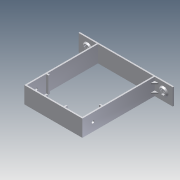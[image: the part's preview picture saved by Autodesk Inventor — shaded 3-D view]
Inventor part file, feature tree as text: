
AUTODESK INVENTOR PART (.ipt)
format: ipt  version: 2011 (Build 150239000, 239)  size: 209,920 bytes
history: native  units: mm
features: extrude x5, sketch x5, plane x1, rib x1, pattern_linear x1, draft x1, mirror x1
ambient origin geometry x8: Origin, YZ Plane, XZ Plane, XY Plane, X Axis, Y Axis, Z Axis, Center Point
bodies: Solid1 (feature_tree)
feature tree (15):
  extrude  "Extrusion1"  Depth=1.75mm
  extrude  "Extrusion2"  Depth=22.75mm
  extrude  "Extrusion3"  Depth=36.5mm
  plane  "Work Plane1"
  rib  "Rib1"
  pattern_linear  "Rectangular Pattern1"  Spacing1=21.0mm  [1 undecoded]
  sketch  "Sketch6"  dims[d9=3.4mm d10=21.0mm d11=0.0mm d12=23.3mm d13=3.4mm d14=21.0mm d15=0.0mm d16=1.75mm d17=3.0mm d18=21.6mm d21=5.25mm d22=45.0deg d24=1.0mm d25=1.75mm d26=0.0mm d27=20.0mm d29=10.5mm d30=4.5mm d31=1.75mm d32=5.6mm d33=1.5mm d34=0.75mm d35=0.0mm d36=1.55mm d37=0.0mm d38=45.0deg d39=1.75mm d40=3.0mm d41=23.9mm]
  extrude  "Extrusion5"  Depth=23.3mm
  extrude  "Extrusion6"  Depth=3.4mm
  draft  "FaceDraft1"
  mirror  "Mirror5"
  sketch  "Sketch1"  dims[d0=1.75mm d1=1.75mm]
  sketch  "Sketch2"  dims[d2=1.75mm d4=22.75mm]
  sketch  "Sketch3"  dims[d5=21.0mm d6=0.0mm d7=36.5mm]
  sketch  "Sketch5"  dims[d8=92.69mm]
note: 1 required parameter value undecoded (feature->parameter linkage not recoverable at this tier; creation-order binding heuristic only, values carry confidence <= 0.55)
